# Revit family: Bottle_Filler-Sloan-Valve-DRS100-FIL-REF-SSz
name_source: partatom
category: Plumbing Fixtures
units: mm (PartAtom-declared; Revit-internal decimal feet)

## family parameters
Cut with Voids When Loaded = Yes
Host = Face
OmniClass Number = 23.45.05.00
OmniClass Title = Sanitary Equipment
Part Type = Normal
Room Calculation Point = No
Round Connector Dimension = Use Diameter
Shared = No

## types (1)
- Refer to Type Catalog
    ADA Compliant = Yes
    Apparent Load = 240 VA
    Assembly Code = D2010810
    CW Connection = Yes
    CWFU = 1.2
    Cold Water Connection Diameter = 3/8"
    Cold Water Connector Description = Cold Water Connector
    Connector Description = Electrical Connection
    Current = 5 A
    Default Elevation = 0"
    Depth = 8"
    Description = Sloan DropSpot™ On-wall Bottle Filler, Filtered, Refrigerated, Stainless.
    Filter option = Yes
    Frequency = 60 Hz
    HW Connection = No
    HWFU = 0
    Height = 52 7/8"
    Manufacturer = Sloan Valve
    Model = DRS100-FIL-REF-SS - With Refrigeration
    Number of Poles = 3
    Part Number = 33820004
    Power Factor = 0.8
    Product Material = Sloan Valve - Finish - Stainless Steel
    Refrigeration option = Yes
    Sanitary Drain Connection Diameter = 1 1/4"
    Sanitary Drain Connector Description = Sanitary Drain Connector
    URL = www.sloanvalve.com
    Vent Connection = No
    Version = 1
    VoidOffset = 10 31/32"
    Voltage = 115 V
    WFU = 2
    Waste Connection = Yes
    Water Flow = 1.2 GPM
    Weight = 77.00 lb
    Width = 19 1/32"

## geometry (parser evidence)
native form markers: Sweep x4
no freeform markers — native parametric forms only
